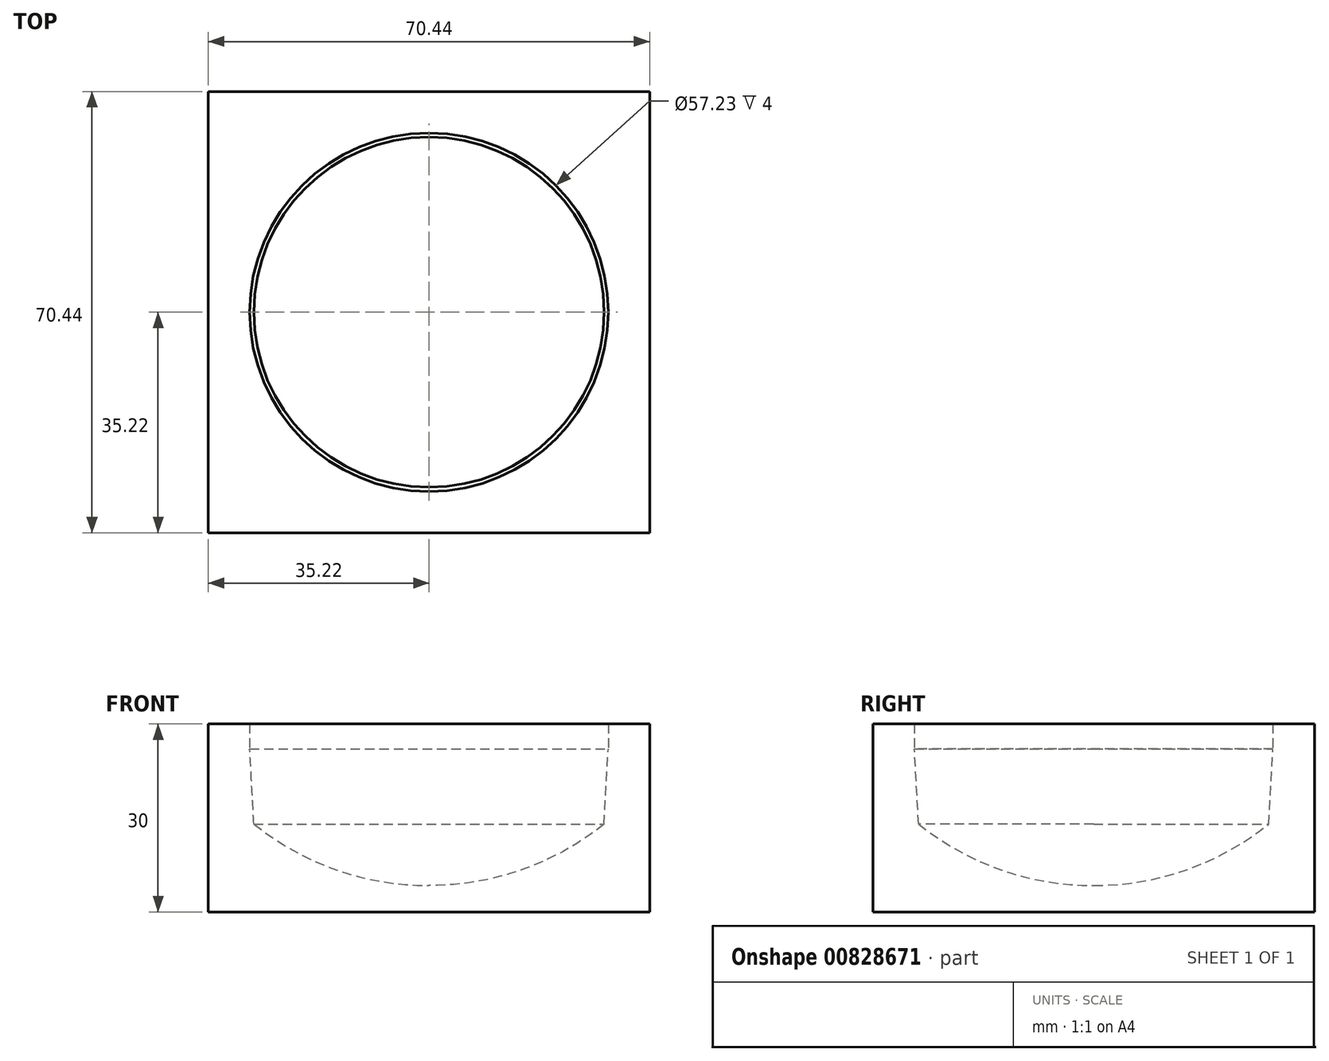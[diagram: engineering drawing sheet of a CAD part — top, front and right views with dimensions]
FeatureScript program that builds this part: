
annotation { "Feature Type Name" : "Feature", "Feature Type Description" : "" }
export const myFeature = defineFeature(function(context is Context, id is Id, definition is map)
    precondition{}
    {
        {
            var Q0;
            Q0=qCreatedBy(makeId("Top.planeOp"),FACE);
            var sketch = newSketch(context, id + "F0", { "sketchPlane" : qUnion([Q0])});
            skLineSegment(sketch, "E0.bottom", {"start": v(-35.22, 35.22) * mm, "end": v(35.22, 35.22) * mm});
            skLineSegment(sketch, "E0.top", {"start": v(-35.22, -35.22) * mm, "end": v(35.22, -35.22) * mm});
            skLineSegment(sketch, "E0.left", {"start": v(-35.22, 35.22) * mm, "end": v(-35.22, -35.22) * mm});
            skLineSegment(sketch, "E0.right", {"start": v(35.22, 35.22) * mm, "end": v(35.22, -35.22) * mm});
            skPoint(sketch, "E0.middle", {"position": v(0, 0) * mm});
            skSolve(sketch);
        }
        {
            var Q0;
            Q0 = qSketchRegion(id + "F0", true);
            var Q1;
            Q1 = qSketchRegion(id + "F2", true);
            extrude(context, id + "F1", {"entities" : qUnion([Q0, Q1]), "oppositeDirection" : true, "depth" : 30 * mm, "offsetDistance" : 25 * mm});
        }
        {
            var Q0;
            Q0=qCreatedBy(makeId("Front.planeOp"),FACE);
            var sketch = newSketch(context, id + "F2", { "sketchPlane" : qUnion([Q0])});
            skLineSegment(sketch, "E1", {"start": v(0, -16) * mm, "end": v(27.95, -16) * mm, "construction": true});
            skLineSegment(sketch, "E2", {"start": v(0, -16) * mm, "end": v(0, -7) * mm});
            skLineSegment(sketch, "E3", {"start": v(0, -16) * mm, "end": v(0, -25.8) * mm});
            skLineSegment(sketch, "E4", {"start": v(0, -7) * mm, "end": v(28.45, -7) * mm, "construction": true});
            skLineSegment(sketch, "E5", {"start": v(27.95, -16) * mm, "end": v(28.45, -7) * mm});
            skArc(sketch, "E6", {"start": v(0, -25.8) * mm, "mid": v(14.8, -23.28) * mm, "end": v(27.95, -16) * mm});
            skLineSegment(sketch, "E7", {"start": v(27.95, -16) * mm, "end": v(28.62, -4) * mm});
            skLineSegment(sketch, "E8", {"start": v(0, -7) * mm, "end": v(0, -4) * mm});
            skLineSegment(sketch, "E9", {"start": v(0, -4) * mm, "end": v(28.62, -4) * mm, "construction": true});
            skLineSegment(sketch, "E10", {"start": v(28.62, -4) * mm, "end": v(28.62, 0) * mm});
            skLineSegment(sketch, "E11", {"start": v(0, -4) * mm, "end": v(0, 0) * mm});
            skLineSegment(sketch, "E12", {"start": v(0, 0) * mm, "end": v(28.62, 0) * mm});
            skSolve(sketch);
        }
        {
            var Q0;
            Q0 = qSketchRegion(id + "F2", true);
            var Q1;
            Q1=sQuery(id+"F2.wireOp",EDGE,"E2");
            revolve(context, id + "F3", {"operationType" : NewBodyOperationType.REMOVE, "surfaceOperationType" : NewSurfaceOperationType.NEW, "entities" : qUnion([Q0]), "axis" : qUnion([Q1]), "revolveType" : RevolveType.FULL});
        }
    });
